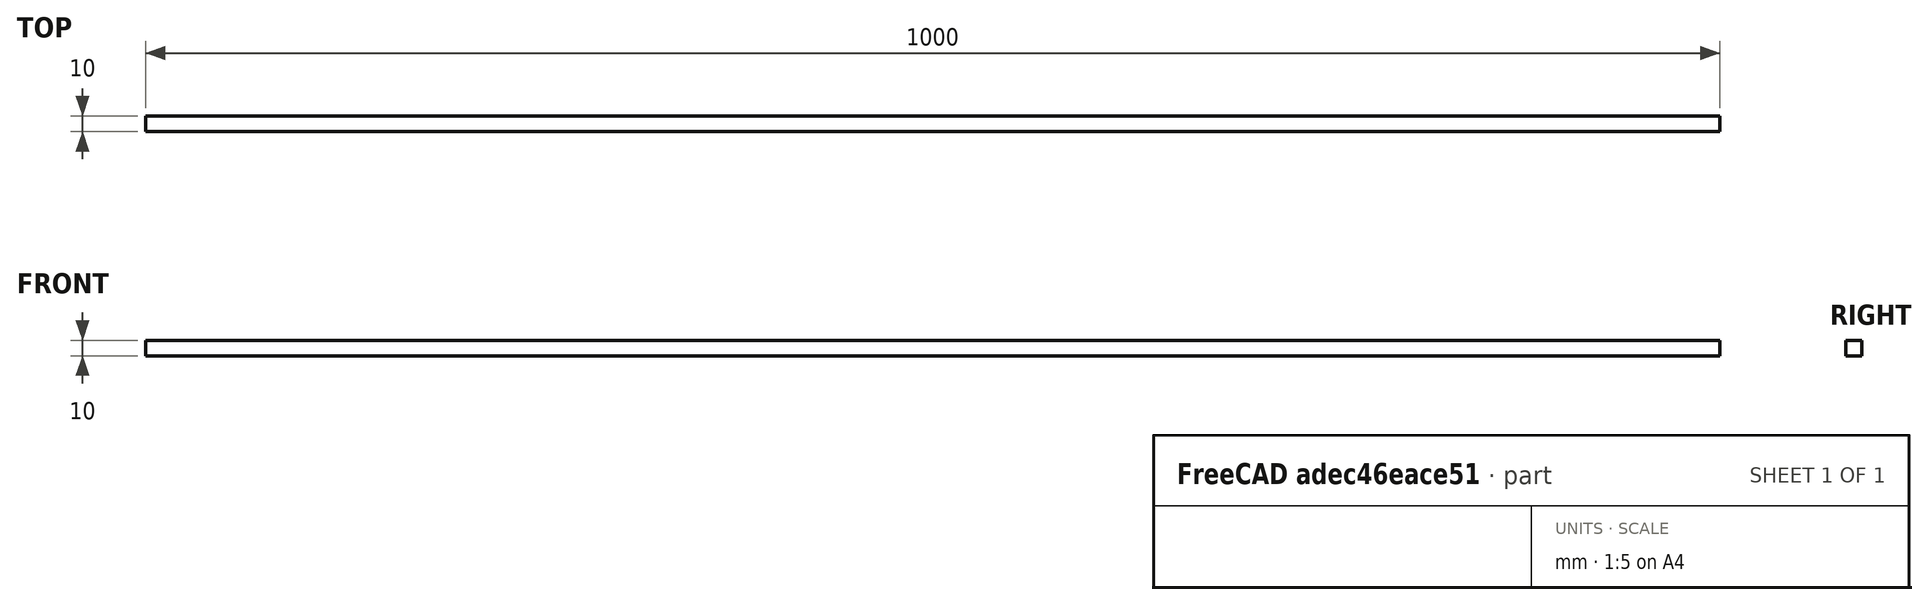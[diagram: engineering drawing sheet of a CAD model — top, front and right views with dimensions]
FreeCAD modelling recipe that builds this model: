
FCSTD DOCUMENT  (FreeCAD 0.21R33694 (Git))
Label: buckling_test
License: All rights reserved
LicenseURL: http://en.wikipedia.org/wiki/All_rights_reserved
objects: Part::Box×1, Fem::ConstraintForce×1, App::MaterialObjectPython×1, Fem::FemMeshObjectPython×1, Fem::ConstraintFixed×1, Fem::FemSolverObjectPython×1, Fem::FemAnalysis×1
note: 1 computed .brp shape members not serialized (recipe doc carries the construction recipe); baked Part::Feature solids carry a one-line shape summary decoded from their .brp

FEATURE [Part::Box] Box  label="Cube"
  AttacherType = Attacher::AttachEngine3D
  Height = 10
  Length = 1000
  Width = 10
FEATURE [Fem::ConstraintForce] ConstraintForce
  DirectionVector = (-1,0,0)
  Force = 1
  NormalDirection = (1,0,0)
  Points = (9) [(1000,10,0),(1000,10,5),(1000,10,10),(1000,5,0),(1000,5,5),(1000,5,10),(1000,0,0),(1000,0,5),(1000,0,10)]
  References = -> [Box]
  Reversed = true
FEATURE [App::MaterialObjectPython] MaterialSolid  # material (typed FeaturePython)
  Category = 0
  Material = AuthorAndLicense=(c) 2014 M. Münch - GNU Lesser General Public License (LGPL); CardName=Steel-St-E-315; Density=7800 kg/m^3; Father=Metal; KindOfMaterial=Fine grain steel; KindOfMaterialDE=Feinkornstahl; MaterialNumber=1.0505; Name=St E 315; NameDE=St E 315; Norm=DIN 17102; PoissonRatio=0.0; ShearModulus=81000 MPa; ThermalExpansionCoefficient=0.000011 m/m/K; UltimateStrain=0; UltimateTensileStrength=440 MPa; YieldStrength=320 MPa; YoungsModulus=100000000.0 kPa
FEATURE [Fem::FemMeshObjectPython] FEMMeshGmsh  # FEM object (typed FeaturePython)
  Algorithm2D = 0
  Algorithm3D = 0
  CharacteristicLengthMax = 100
  CharacteristicLengthMin = 100
  CoherenceMesh = true
  ElementDimension = 0
  ElementOrder = 1
  GeometryTolerance = 1e-06
  GroupsOfNodes = false
  HighOrderOptimize = 0
  MeshSizeFromCurvature = 12
  OptimizeNetgen = false
  OptimizeStd = true
  Part = -> Box
  RecombinationAlgorithm = 0
  Recombine3DAll = false
  RecombineAll = false
  SecondOrderLinear = false
FEATURE [Fem::ConstraintFixed] ConstraintFixed
  NormalDirection = (-1,0,0)
  Normals = (9) [(-1,0,0),(-1,0,0),(-1,0,0),(-1,0,0),(-1,0,0),(-1,0,0),(-1,0,0),(-1,0,0),(-1,0,0)]
  Points = (9) [(0,10,0),(0,10,5),(0,10,10),(0,5,0),(0,5,5),(0,5,10),(0,0,0),(0,0,5),(0,0,10)]
  References = -> [Box]
FEATURE [Fem::FemSolverObjectPython] SolverCcxTools  # FEM object (typed FeaturePython)
  AnalysisType = 0
  BeamShellResultOutput3D = false
  BucklingFactors = 1
  EigenmodeHighLimit = 1000000
  EigenmodeLowLimit = 0
  EigenmodesCount = 10
  GeometricalNonlinearity = 0
  IterationsControlParameterCutb = 0.25,0.5,0.75,0.85,,,1.5,
  IterationsControlParameterIter = 4,8,9,200,10,400,,200,,
  IterationsControlParameterTimeUse = false
  IterationsThermoMechMaximum = 2000
  IterationsUserDefinedIncrementations = false
  IterationsUserDefinedTimeStepLength = false
  MaterialNonlinearity = 0
  MatrixSolverType = 0
  SplitInputWriter = false
  ThermoMechSteadyState = true
  TimeEnd = 1
  TimeInitialStep = 0.01
FEATURE [Fem::FemAnalysis] Analysis
  Group = -> [ConstraintForce,MaterialSolid,FEMMeshGmsh,ConstraintFixed,SolverCcxTools]
